# Revit family: Bright 3.F
name_source: partatom
category: Lighting Fixtures
revit_build: Autodesk Revit 2017 (Build: 20170419_0315(x64)
units: mm (PartAtom-declared; Revit-internal decimal feet)

## family parameters
Cut with Voids When Loaded = Yes
Host = Face
Light Source = Yes
Part Type = Normal
Room Calculation Point = Yes
Round Connector Dimension = Use Diameter
Shared = No

## types (14) — shared parameters
Apparent Load = 0 VA
Body = L&L_Anodized aluminium
CRI = 90 (also available: CRI 80 - ref. URL Technical sheet)
Code = -
Color Filter = 16777215
Control system = -
Cutout dimensions = diam. 96 mm
Default Elevation = 1219 mm
Delivered lumen output = 911 lm (3000K, 55°, 13W, CRI 90), 845 lm (3000K, 55°, 10W, CRI 80), 759 lm (3000K, 55°, 10W, CRI 90), 1125 lm (3000K, 55°, 13W, CRI 80)
Description = recessed for outdoor applications
Dimming Lamp Color Temperature Shift = <None>
Emit from Line Length = 610 mm
Energy efficiency class = A A+ A++
Features = 16°x69° optics adjustable through 360° using the magnet provided
Geometry = Bright 3.F_mod
Height Void = 80 mm  [stored 0.262467 ft]
Height mm = 75 mm
IP = IP68, IP69K
LED Colour = 3000K (also available: 2700K and 4000K - ref. URL Technical sheet)
Length mm = 112 mm  [stored 0.367454 ft]
Lens = L&L_Tempered extra-clear glass
Lumen output at source = 900 lm (3000K, 10W, CRI 90), 1485 lm (3000K, 13W, CRI 80), 1200 lm (3000K, 13W, CRI 90), 1115 lm (3000K, 10W, CRI 80)
Manufacturer = L&L Luce&Light
Material = body in anodized aluminium, trim in AISI 316L stainless steel, screen in tempered, serigraphed-grey and transparent extra-clear glass
Model = Bright 3.F
Mounting = recessed (ceiling, wall, floor)
No. and type of led = 1 high power density COB LED, 3-step MacAdam, 50 000h L95 B10 (Ta 25°C)
Notes = -
Power Supply = L&L_Steel inox AISI 316L
Power cables = includes 1,50 m neoprene cable, H05RN-F 2x0,75/0,75 Ø6,3 mm
Power supply = 24Vdc
Power supply unit = not included
Radius Void = 50 mm  [stored 0.164042 ft]
Tilt Angle = 90.00°
Tiltable = -
Trim = L&L_Steel inox AISI 316L
URL = https://www.lucelight.it
URL Accessories and power supply units = https://www.lucelight.it
URL Catalogue = https://www.lucelight.it
URL DXF = https://www.lucelight.it
URL Description = https://www.lucelight.it
URL General code = https://www.lucelight.it
URL IES Photometric file = https://www.lucelight.it
URL Image = https://www.lucelight.it
URL Technical sheet = https://www.lucelight.it
Voltage = 24 V
Weight kg = 0.78 kg
Width mm = 112 mm  [stored 0.367454 ft]
Wiring = parallel

## per-type parameters (varying)
| type | Apparent Load Phase 1 | Optics | Photometric Web File | Power |
| Bright 3.F D (3000K 10W 24Vdc) | 10 W | D | BRIGHT 3.F D [3000K 10W 24Vdc].IES | 10W |
| Bright 3.F K 55° (3000K 10W 24Vdc) | 10 W | 55° | BRIGHT 3.F K 55° [3000K 10W 24Vdc].IES | 10W |
| Bright 3.F L 38° (3000K 10W 24Vdc) | 10 W | 38° | BRIGHT 3.F L 38° [3000K 10W 24Vdc].IES | 10W |
| Bright 3.F P 58° (3000K 10W 24Vdc) | 10 W | 58° | BRIGHT 3.F P (58°) [3000K 10W 24Vdc].IES | 10W |
| Bright 3.F S 16° (3000K 10W 24Vdc) | 10 W | 16° | BRIGHT 3.F S 16° [3000K 10W 24Vdc].IES | 10W |
| Bright 3.F W 16°x69° magnet (3000K 10W 24Vdc) | 10 W | 16°x69° adjustable through 360° | BRIGHT 3.F W 16°x69° magnet [3000K 10W 24Vdc].IES | 10W |
| Bright 3.F D (3000K 13W 24Vdc) | 13 W | D | BRIGHT 3.F D [3000K 13W 24Vdc].IES | 13W |
| Bright 3.F K 55° (3000K 13W 24Vdc) | 13 W | 55° | BRIGHT 3.F K 55° [3000K 13W 24Vdc].IES | 13W |
| Bright 3.F L 38° (3000K 13W 24Vdc) | 13 W | 38° | BRIGHT 3.F L 38° [3000K 13W 24Vdc].IES | 13W |
| Bright 3.F M 21° (3000K 13W 24Vdc) | 13 W | 21° | BRIGHT 3.F M 21° [3000K 13W 24Vdc].IES | 13W |
| Bright 3.F P 58° (3000K 13W 24Vdc) | 13 W | 58° | BRIGHT 3.F P (58°) [3000K 13W 24Vdc].IES | 13W |
| Bright 3.F S 16° (3000K 13W 24Vdc) | 13 W | 16° | BRIGHT 3.F S 16° [3000K 13W 24Vdc].IES | 13W |
| Bright 3.F W 16°x69° magnet (3000K 13W 24Vdc) | 13 W | 16°x69° adjustable through 360° | BRIGHT 3.F W 16°x69° magnet [3000K 13W 24Vdc].IES | 13W |
| Bright 3.F M 21° (3000K 10W 24Vdc) | 10 W | 21° | BRIGHT 3.F M 21° [3000K 10W 24Vdc].IES | 10W |

note: [stored X ft] marks values corroborated as IEEE doubles in the binary element streams (Revit-internal decimal feet)

## geometry (parser evidence)
native form markers: Blend x2, Sweep x8
no freeform markers — native parametric forms only
